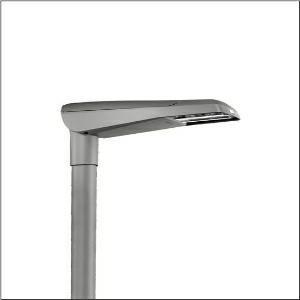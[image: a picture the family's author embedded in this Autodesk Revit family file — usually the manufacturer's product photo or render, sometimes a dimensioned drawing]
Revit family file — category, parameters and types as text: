
# Revit family: streetlight_sl_11_iq_micro___st1_2a_5xc1ac1f08de_2d80
name_source: partatom
category: Lighting Fixtures
units: mm (PartAtom-declared; Revit-internal decimal feet)

## family parameters
Cut with Voids When Loaded = No
Host = Face
Light Source = No
Part Type = Normal
Room Calculation Point = No
Round Connector Dimension = Use Diameter
Shared = No

## types (1)
- --- (1 x LED, 3860 lm, 27.4 W, 4000K)
    Apparent Load = 27 VA
    CIE Flux Codes = 33 71 96 100 100
    Color Rendering = 70
    Color Temperature = 4000K
    Default Elevation = 1800 mm
    Description = Streetlight SL 11 iQ micro, mast luminaire, primary light control with 3 zone facetted reflector, of plastic, silver coated, highly specular, primary optical cover: cover, of PMMA, transparent, light distribution: ST1.2a, light emission: direct distribution, primary light characteristic: asymmetric, installation type: post-top, side-entry, lamps: LED, High Power LED, rated values: 3.620lm | 27,7W | 130,7lm/W (begin service life); end service life: 3.620lm | 28,1W; at 50% lumin. flux: 1.810lm | 13,4W | 135,1lm/W, colour temperature: 2200/2700/3000/4000K, colour rendering: CRI > 70, light colour: 722/727/730/740, light setting 1 begin service life: 100% | 3.620lm | 27,7W | 130,7lm/W | 3.000K, light setting 1 end service life: 28,1W, further light settings possible, control: Street-Remote, Auto-Match, Temp-Guard, Lumen-Switch, Night-Set, Smart-Wire, Light-Fading, Desk-Remote (wireless, voltage-free reading and setting of iQ features in the workshop via application-optimized NFC function/RFID function), optimised constant luminous flux control (CLO 2.0), with cable H07RN-F 5x 1.5mm², mains connection: 220..240V, AC, 50/60Hz, connection cable pre-assembled, cable length: 6,5m, luminaire housing, of diecast aluminium, powder-coated, Siteco® metallic grey (DB 702S), please order mast flange separately, inclination adjustable without tools: 0°, 5°, 10°, 15° (post-top) | 0°, -5°, -10°, -15° (side-entry), sealing non-destructively replaceable, multi-level sealing system, length: 600mm, width: 174mm, height: 116mm, mast flange for spigot size: 42mm (side-entry): 5XC10008XM4, 60/48mm (side-entry/post-top): 5XC10108XM2, 76/60mm (side-entry/post-top): 5XC10108XM1, equipment: Power, protection rating (complete): IP66, insulation class (complete): insulation class II (safety insulation), certification: CE, ENEC, ENEC+, VDE, impact resistance: IK10, permissible operating ambient temperature for outdoor applications: -25..+50°C, standard-compliant lighting for roads and squares, Environmental Product Declaration (EPD) tested and certified by an independent institute, packaging unit: 1 piece

Light Distribution: ST1.2a
    Height = 116 mm
    Lamp = 1 x LED
    Lamp Light Flux = 3860 lm
    Lamp Power = 27.4 W
    Lamp count = 1
    Length = 600 mm
    Luminous efficacy = 141 lm/W
    Manufacturer = Siteco
    ModVariant = No
    Model = 5XC1AC1F08DE
    Number of Poles = 1
    OnlyDefault = Yes
    Power Factor = 1
    Product Name = Streetlight SL 11 iQ micro | ST1.2a
    Product group = mast luminaire | pylon top
    ProductGroupID = 6100
    Protection Class = Protection class II
    Protection Degree = IP 66
    RLX_Detail_Level = 1
    RLX_Emergency_Light_Flux = 0 lm
    RLX_Emergency_Type = 0
    RLX_Emergency_Type_DB = No
    RlxData = <blob elided: 59937 chars, md5=6954c1d6>
    Socket = socket
    Standby Power = 0 W
    System Light Flux = 3860 lm
    System Power = 27 W
    Type Comments = individual setting: luminous flux: 100 % | dim-lin: 254 | 726 mA
    Type Image = l_1006566.jpg
    URL = http://relux.com
    VarID = @adj_060875
    Voltage = 0 V
    Weight = 0.00 kg
    Width = 174 mm

## geometry (parser evidence)
native form markers: Blend x4, Sweep x12
no freeform markers — native parametric forms only
